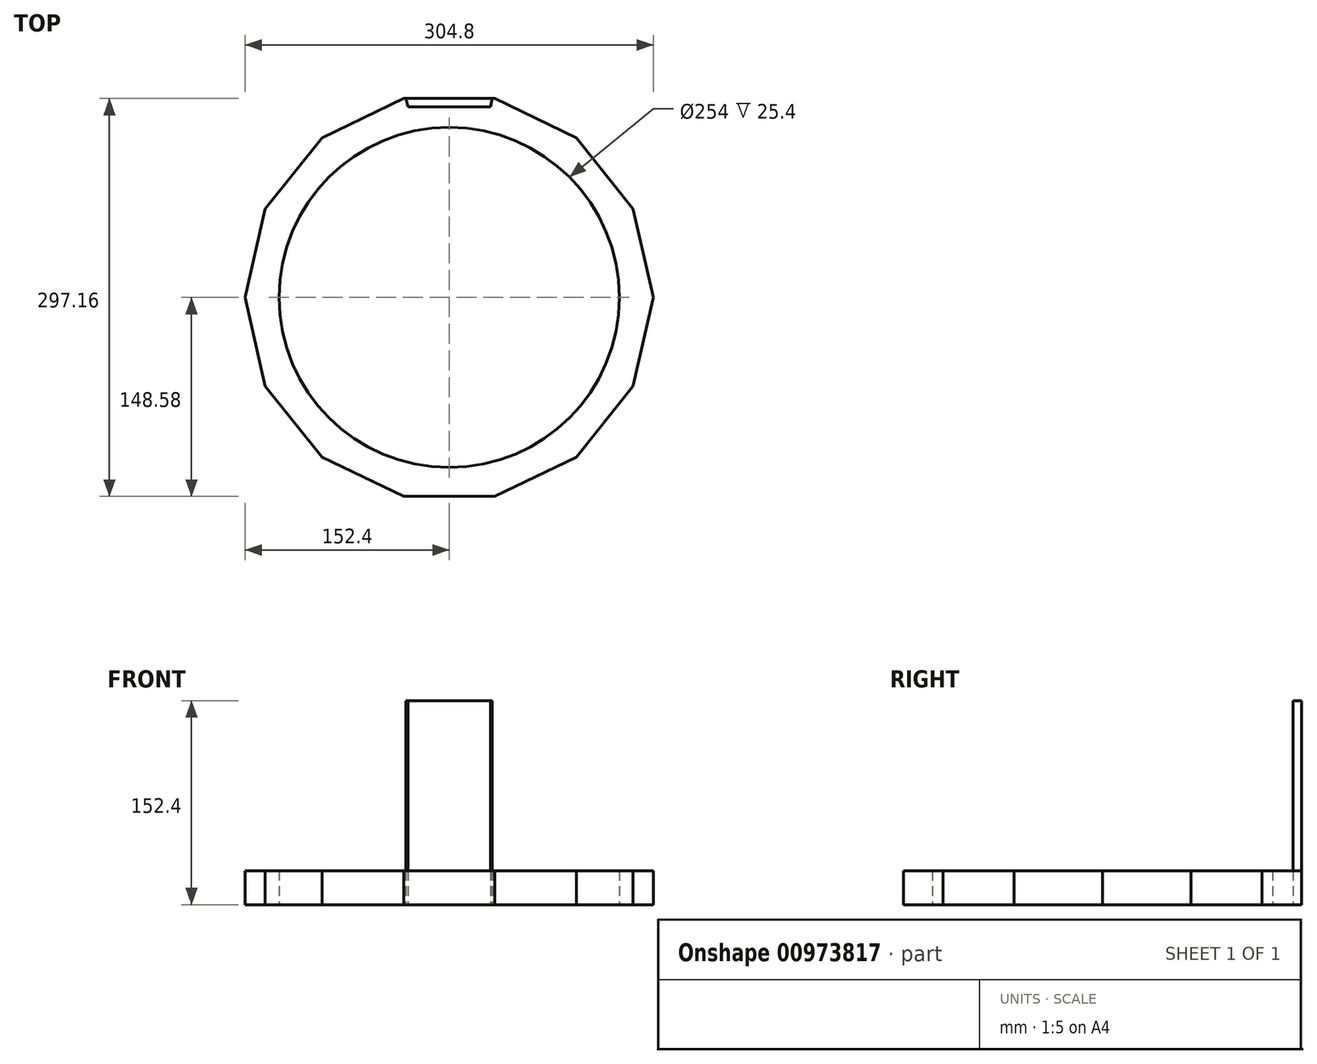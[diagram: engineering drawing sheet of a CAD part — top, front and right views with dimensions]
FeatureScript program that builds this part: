
annotation { "Feature Type Name" : "Feature", "Feature Type Description" : "" }
export const myFeature = defineFeature(function(context is Context, id is Id, definition is map)
    precondition{}
    {
        {
            var Q0;
            Q0=qCreatedBy(makeId("Top.planeOp"),FACE);
            var sketch = newSketch(context, id + "F0", { "sketchPlane" : qUnion([Q0])});
            skCircle(sketch, "E0.cCircle", {"center": v(0, 0) * mm, "radius": 152.4 * mm, "construction": true});
            skLineSegment(sketch, "E0.0", {"start": v(137.3, -66.12) * mm, "end": v(95.02, -119.15) * mm});
            skLineSegment(sketch, "E0.1", {"start": v(95.02, -119.15) * mm, "end": v(33.91, -148.58) * mm});
            skLineSegment(sketch, "E0.2", {"start": v(33.91, -148.58) * mm, "end": v(-33.91, -148.58) * mm});
            skLineSegment(sketch, "E0.3", {"start": v(-33.91, -148.58) * mm, "end": v(-95.02, -119.15) * mm});
            skLineSegment(sketch, "E0.4", {"start": v(-95.02, -119.15) * mm, "end": v(-137.3, -66.12) * mm});
            skLineSegment(sketch, "E0.5", {"start": v(-137.3, -66.12) * mm, "end": v(-152.4, 0) * mm});
            skLineSegment(sketch, "E0.6", {"start": v(-152.4, 0) * mm, "end": v(-137.3, 66.12) * mm});
            skLineSegment(sketch, "E0.7", {"start": v(-137.3, 66.12) * mm, "end": v(-95.02, 119.15) * mm});
            skLineSegment(sketch, "E0.8", {"start": v(-95.02, 119.15) * mm, "end": v(-33.91, 148.58) * mm});
            skLineSegment(sketch, "E0.9", {"start": v(-33.91, 148.58) * mm, "end": v(33.91, 148.58) * mm});
            skLineSegment(sketch, "E0.10", {"start": v(33.91, 148.58) * mm, "end": v(95.02, 119.15) * mm});
            skLineSegment(sketch, "E0.11", {"start": v(95.02, 119.15) * mm, "end": v(137.3, 66.12) * mm});
            skLineSegment(sketch, "E0.12", {"start": v(137.3, 66.12) * mm, "end": v(152.4, 0) * mm});
            skLineSegment(sketch, "E0.13", {"start": v(152.4, 0) * mm, "end": v(137.3, -66.12) * mm});
            skCircle(sketch, "E1.cCircle", {"center": v(0, 0) * mm, "radius": 146.05 * mm, "construction": true});
            skLineSegment(sketch, "E1.0", {"start": v(-146.05, 0) * mm, "end": v(-131.59, 63.37) * mm});
            skLineSegment(sketch, "E1.1", {"start": v(-131.59, 63.37) * mm, "end": v(-91.06, 114.19) * mm});
            skLineSegment(sketch, "E1.2", {"start": v(-91.06, 114.19) * mm, "end": v(-32.5, 142.39) * mm});
            skLineSegment(sketch, "E1.3", {"start": v(-32.5, 142.39) * mm, "end": v(32.5, 142.39) * mm});
            skLineSegment(sketch, "E1.4", {"start": v(32.5, 142.39) * mm, "end": v(91.06, 114.19) * mm});
            skLineSegment(sketch, "E1.5", {"start": v(91.06, 114.19) * mm, "end": v(131.59, 63.37) * mm});
            skLineSegment(sketch, "E1.6", {"start": v(131.59, 63.37) * mm, "end": v(146.05, 0) * mm});
            skLineSegment(sketch, "E1.7", {"start": v(146.05, 0) * mm, "end": v(131.59, -63.37) * mm});
            skLineSegment(sketch, "E1.8", {"start": v(131.59, -63.37) * mm, "end": v(91.06, -114.19) * mm});
            skLineSegment(sketch, "E1.9", {"start": v(91.06, -114.19) * mm, "end": v(32.5, -142.39) * mm});
            skLineSegment(sketch, "E1.10", {"start": v(32.5, -142.39) * mm, "end": v(-32.5, -142.39) * mm});
            skLineSegment(sketch, "E1.11", {"start": v(-32.5, -142.39) * mm, "end": v(-91.06, -114.19) * mm});
            skLineSegment(sketch, "E1.12", {"start": v(-91.06, -114.19) * mm, "end": v(-131.59, -63.37) * mm});
            skLineSegment(sketch, "E1.13", {"start": v(-131.59, -63.37) * mm, "end": v(-146.05, 0) * mm});
            skLineSegment(sketch, "E2", {"start": v(-152.4, 0) * mm, "end": v(152.4, 0) * mm, "construction": true});
            skPoint(sketch, "E3", {"position": v(-30.87, 142.39) * mm});
            skPoint(sketch, "E4", {"position": v(24.18, 142.39) * mm});
            skPoint(sketch, "E5", {"position": v(-33.97, 141.68) * mm});
            skLineSegment(sketch, "E6", {"start": v(-33.97, 141.68) * mm, "end": v(-30.87, 142.39) * mm, "construction": true});
            skLineSegment(sketch, "E7", {"start": v(-33.97, 141.68) * mm, "end": v(-35.38, 147.87) * mm});
            skLineSegment(sketch, "E8", {"start": v(-30.87, 142.39) * mm, "end": v(-32.28, 148.58) * mm});
            skLineSegment(sketch, "E9", {"start": v(-33.97, 141.68) * mm, "end": v(-32.5, 142.39) * mm});
            skLineSegment(sketch, "E10", {"start": v(-32.5, 142.39) * mm, "end": v(-30.87, 142.39) * mm});
            skLineSegment(sketch, "E11", {"start": v(-32.5, 142.39) * mm, "end": v(-33.91, 148.58) * mm, "construction": true});
            skLineSegment(sketch, "E12", {"start": v(-35.38, 147.87) * mm, "end": v(-33.83, 148.23) * mm, "construction": true});
            skLineSegment(sketch, "E13", {"start": v(-33.83, 148.23) * mm, "end": v(-32.28, 148.58) * mm, "construction": true});
            skLineSegment(sketch, "E14", {"start": v(33.91, 148.58) * mm, "end": v(32.5, 142.39) * mm, "construction": true});
            skLineSegment(sketch, "E15", {"start": v(32.24, 148.58) * mm, "end": v(30.83, 142.39) * mm});
            skLineSegment(sketch, "E16", {"start": v(35.42, 147.85) * mm, "end": v(34, 141.66) * mm});
            skLineSegment(sketch, "E17", {"start": v(32.24, 148.58) * mm, "end": v(33.83, 148.22) * mm, "construction": true});
            skLineSegment(sketch, "E18", {"start": v(33.83, 148.22) * mm, "end": v(35.42, 147.85) * mm, "construction": true});
            skLineSegment(sketch, "E19", {"start": v(30.83, 142.39) * mm, "end": v(34, 141.66) * mm, "construction": true});
            skCircle(sketch, "E20", {"center": v(0, 0) * mm, "radius": 127 * mm});
            skSolve(sketch);
        }
        {
            var Q0;
            {var subQ0=sQuery(id+"F0.wireOp",EDGE,"E8");Q0=makeQuery(id+"F0.imprint","IMPRINT",FACE,{"disambiguationData":[TD([[makeQuery(id+"F0.imprint","IMPRINT",EDGE,{"derivedFrom":subQ0}),-1.0]])]});}
            var Q1;
            Q1=makeQuery(id+"F0.imprint","IMPRINT",FACE,{"disambiguationData":[TD([[makeQuery(id+"F0.imprint","IMPRINT",EDGE,{"derivedFrom":sQuery(id+"F0.wireOp",EDGE,"E0.0")}),-1.0]])]});
            var Q2;
            Q2=makeQuery(id+"F0.imprint","IMPRINT",FACE,{"disambiguationData":[TD([[makeQuery(id+"F0.imprint","IMPRINT",EDGE,{"derivedFrom":sQuery(id+"F0.wireOp",EDGE,"E1.0")}),-1.0]])]});
            var Q3;
            {var subQ7=sQuery(id+"F0.wireOp",EDGE,"E15");Q3=makeQuery(id+"F0.imprint","IMPRINT",FACE,{"disambiguationData":[TD([[makeQuery(id+"F0.imprint","IMPRINT",EDGE,{"derivedFrom":subQ7}),1.0]])]});}
            var Q4;
            {var subQ4=sQuery(id+"F0.wireOp",EDGE,"E7");Q4=makeQuery(id+"F0.imprint","IMPRINT",FACE,{"disambiguationData":[TD([[makeQuery(id+"F0.imprint","IMPRINT",EDGE,{"derivedFrom":subQ4}),-1.0]])]});}
            var Q5;
            Q5=makeQuery(id+"F0.imprint","IMPRINT",FACE,{"disambiguationData":[TD([[makeQuery(id+"F0.imprint","IMPRINT",EDGE,{"derivedFrom":sQuery(id+"F0.wireOp",EDGE,"E20")}),1.0]])]});
            extrude(context, id + "F1", {"entities" : qUnion([Q0, Q1, Q2, Q3, Q4, Q5]), "depth" : 25.4 * mm, "offsetDistance" : 25.4 * mm});
        }
        {
            var Q0;
            {var subQ0=sQuery(id+"F0.wireOp",EDGE,"E8");Q0=makeQuery(id+"F0.imprint","IMPRINT",FACE,{"disambiguationData":[TD([[makeQuery(id+"F0.imprint","IMPRINT",EDGE,{"derivedFrom":subQ0}),-1.0]])]});}
            extrude(context, id + "F2", {"entities" : qUnion([Q0]), "depth" : 152.4 * mm, "offsetDistance" : 25.4 * mm});
        }
        {
            var Q0;
            Q0=makeQuery(id+"F0.imprint","IMPRINT",FACE,{"disambiguationData":[TD([[makeQuery(id+"F0.imprint","IMPRINT",EDGE,{"derivedFrom":sQuery(id+"F0.wireOp",EDGE,"E1.0")}),-1.0]])]});
            var Q1;
            Q1=makeQuery(id+"F0.imprint","IMPRINT",FACE,{"disambiguationData":[TD([[makeQuery(id+"F0.imprint","IMPRINT",EDGE,{"derivedFrom":sQuery(id+"F0.wireOp",EDGE,"E0.0")}),-1.0]])]});
            var Q2;
            {var subQ0=sQuery(id+"F0.wireOp",EDGE,"E8");Q2=makeQuery(id+"F0.imprint","IMPRINT",FACE,{"disambiguationData":[TD([[makeQuery(id+"F0.imprint","IMPRINT",EDGE,{"derivedFrom":subQ0}),-1.0]])]});}
            var Q3;
            {var subQ7=sQuery(id+"F0.wireOp",EDGE,"E15");Q3=makeQuery(id+"F0.imprint","IMPRINT",FACE,{"disambiguationData":[TD([[makeQuery(id+"F0.imprint","IMPRINT",EDGE,{"derivedFrom":subQ7}),1.0]])]});}
            var Q4;
            {var subQ4=sQuery(id+"F0.wireOp",EDGE,"E7");Q4=makeQuery(id+"F0.imprint","IMPRINT",FACE,{"disambiguationData":[TD([[makeQuery(id+"F0.imprint","IMPRINT",EDGE,{"derivedFrom":subQ4}),-1.0]])]});}
            extrude(context, id + "F3", {"entities" : qUnion([Q0, Q1, Q2, Q3, Q4]), "depth" : 25.4 * mm, "offsetDistance" : 25.4 * mm});
        }
    });
